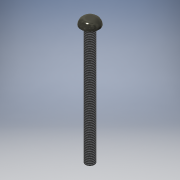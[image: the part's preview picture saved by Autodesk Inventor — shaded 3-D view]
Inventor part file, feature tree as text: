
AUTODESK INVENTOR PART (.ipt)
format: ipt  version: 2016 (Build 200138000, 138)  size: 131,072 bytes
history: native  units: mm
features: extrude x4, sketch x4, other x1, fillet x1, thread x1
ambient origin geometry x1: Origin
bodies: Body1 (feature_tree)
feature tree (11):
  other  "ソリッド1"
  extrude  "押し出し1"  Depth=3.0mm
  extrude  "押し出し2"  Depth=6.0mm TaperAngle=0.0deg
  fillet  "フィレット1"  Radius=6.0mm
  thread  "ねじ1"
  extrude  "押し出し3"  Depth=2.0mm TaperAngle=0.0deg
  extrude  "押し出し4"  Depth=2.0mm
  sketch  "スケッチ1"
  sketch  "スケッチ2"
  sketch  "スケッチ3"
  sketch  "スケッチ4"
